# Revit family: C1100-XR
name_source: partatom
category: Plumbing Fixtures
units: mm (PartAtom-declared; Revit-internal decimal feet)

## family parameters
Classification Number = 23.45.55.21
Cut with Voids When Loaded = No
Enable Cutting in Views = No
Host = Face
Maintain Annotation Orientation = No
Part Type = Normal
Room Calculation Point = No
Round Connector Dimension = Use Radius
Shared = No

## types (3) — shared parameters
Body Height = 2.75 "
Description = FLOOR CLEANOUT WITH HEAVY DUTY ROUND ADJUSTABLE COVEER AND PLUG
Floor Drain Material = Paint - Sherwin Williams Paint - #952C2A - Bellwood Red
Manufacturer = MIFAB
Model = C1100-XR
Stainer Diameter = 8 "
Strainer Radius = 4 "
Top Assembly Height = 1.25 "
URL = WWW.MIFAB.COM
zero-valued in all types: Default Elevation, WFU

## per-type parameters (varying)
| type | Pipe Diameter | Pipe Radius |
| 2" | 2 " | 1 " |
| 3" | 3 " | 1.5 " |
| 4" | 4 " | 2 " |

## geometry (parser evidence)
native form markers: Blend x2, Sweep x2
no freeform markers — native parametric forms only
